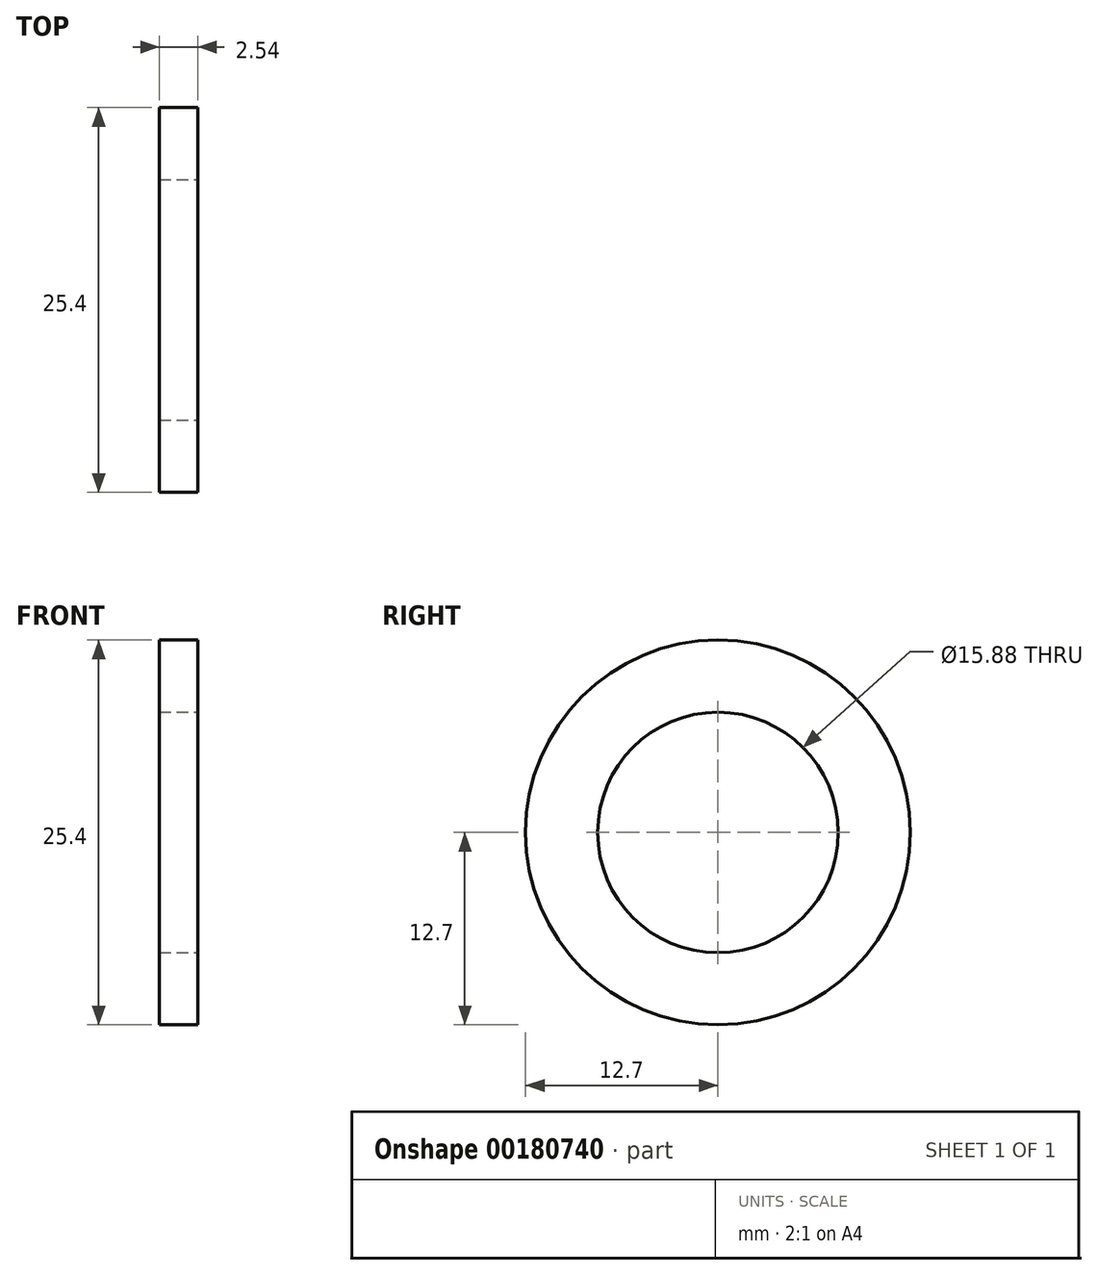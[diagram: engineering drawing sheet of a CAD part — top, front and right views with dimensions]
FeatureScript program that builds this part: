
annotation { "Feature Type Name" : "Feature", "Feature Type Description" : "" }
export const myFeature = defineFeature(function(context is Context, id is Id, definition is map)
    precondition{}
    {
        {
            var Q0;
            Q0=qCreatedBy(makeId("Right.planeOp"),FACE);
            var sketch = newSketch(context, id + "F0", { "sketchPlane" : qUnion([Q0])});
            skCircle(sketch, "E0", {"center": v(0, 0) * mm, "radius": 12.7 * mm});
            skSolve(sketch);
        }
        {
            var Q0;
            Q0 = qSketchRegion(id + "F0", true);
            extrude(context, id + "F1", {"entities" : qUnion([Q0]), "endBound" : BoundingType.SYMMETRIC, "depth" : 2.54 * mm});
        }
        {
            var Q0;
            Q0=makeQuery(id+"F1.opExtrude","CAP_FACE",FACE,{"disambiguationData":[OSD([sQuery(id+"F0.wireOp",EDGE,"E0")])],"isStart":false});
            var sketch = newSketch(context, id + "F2", { "sketchPlane" : qUnion([Q0])});
            skCircle(sketch, "E1", {"center": v(0, 0) * mm, "radius": 7.94 * mm});
            skSolve(sketch);
        }
        {
            var Q0;
            Q0 = qSketchRegion(id + "F2", true);
            extrude(context, id + "F3", {"entities" : qUnion([Q0]), "operationType" : NewBodyOperationType.REMOVE, "endBound" : BoundingType.SYMMETRIC, "oppositeDirection" : true, "depth" : 127 * mm});
        }
    });
